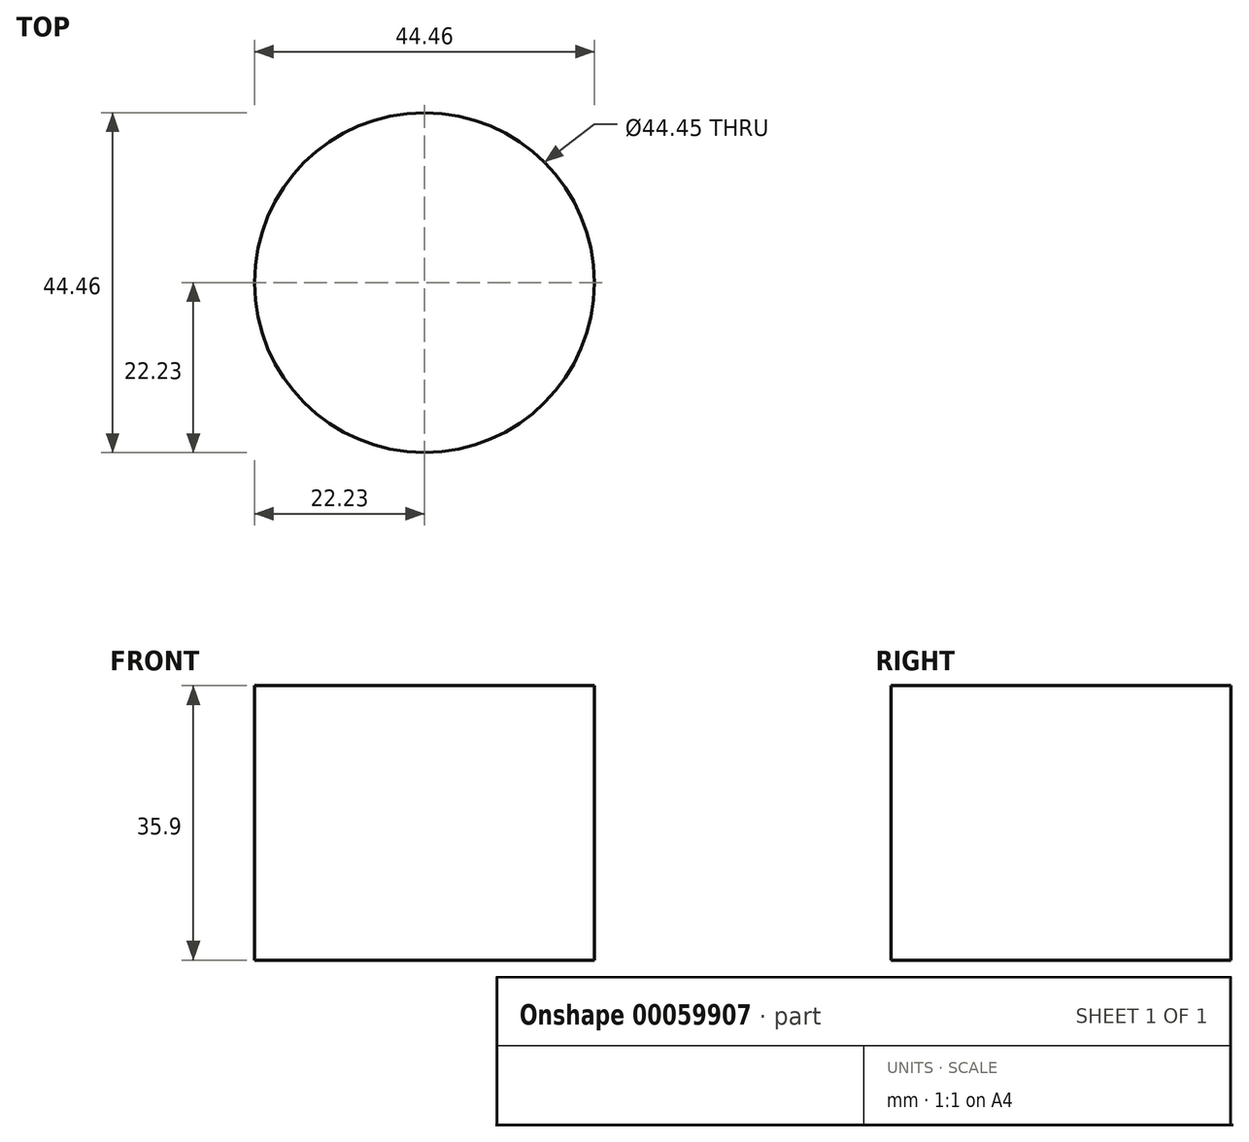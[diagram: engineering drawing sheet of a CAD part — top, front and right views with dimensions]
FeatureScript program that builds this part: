
annotation { "Feature Type Name" : "Feature", "Feature Type Description" : "" }
export const myFeature = defineFeature(function(context is Context, id is Id, definition is map)
    precondition{}
    {
        {
            var Q0;
            Q0=qCreatedBy(makeId("Right.planeOp"),FACE);
            var sketch = newSketch(context, id + "F1", { "sketchPlane" : qUnion([Q0])});
            skLineSegment(sketch, "E0", {"start": v(-22.23, 35.64) * mm, "end": v(-22.23, -0.26) * mm});
            skLineSegment(sketch, "E1.bottom", {"start": v(-22.23, 2.86) * mm, "end": v(0, 2.86) * mm});
            skLineSegment(sketch, "E1.top", {"start": v(-22.23, 0) * mm, "end": v(0, 0) * mm});
            skLineSegment(sketch, "E1.left", {"start": v(-22.23, 2.86) * mm, "end": v(-22.23, 0) * mm});
            skLineSegment(sketch, "E1.right", {"start": v(0, 2.86) * mm, "end": v(0, 0) * mm});
            skSolve(sketch);
        }
        {
            var Q0;
            Q0=sQuery(id+"F1.wireOp",EDGE,"E0");
            var Q1;
            Q1=sQuery(id+"F1.wireOp",EDGE,"E1.right");
            revolve(context, id + "F0", {"bodyType" : ToolBodyType.SURFACE, "surfaceEntities" : qUnion([Q0]), "axis" : qUnion([Q1]), "revolveType" : RevolveType.FULL});
        }
    });
